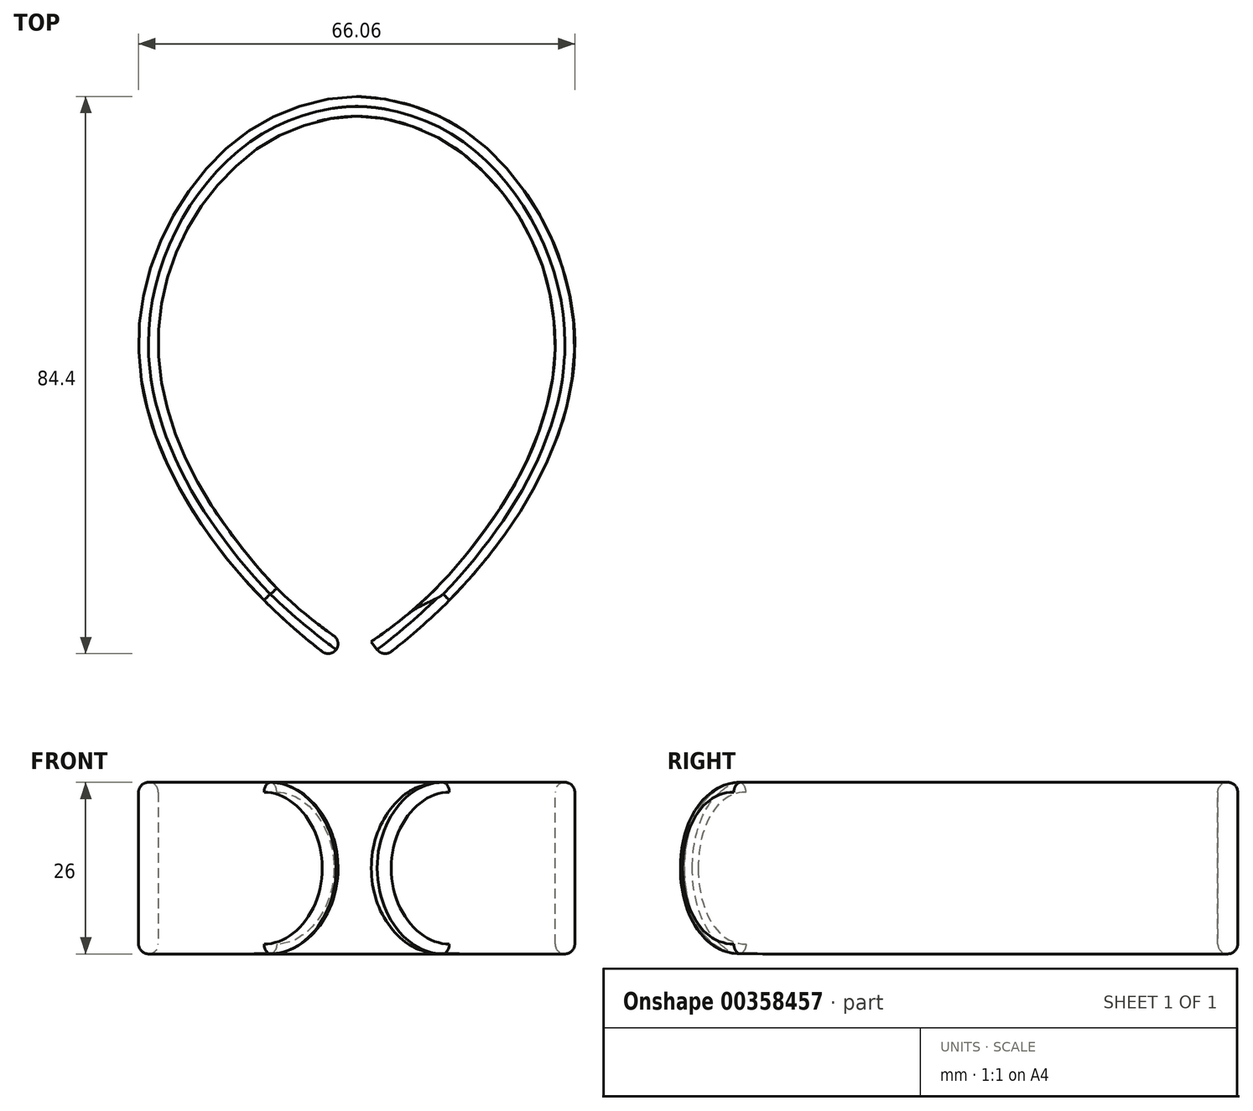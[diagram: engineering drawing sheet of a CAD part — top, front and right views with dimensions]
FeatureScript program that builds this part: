
annotation { "Feature Type Name" : "Feature", "Feature Type Description" : "" }
export const myFeature = defineFeature(function(context is Context, id is Id, definition is map)
    precondition{}
    {
        {
            var Q0;
            Q0=qCreatedBy(makeId("Top.planeOp"),FACE);
            var sketch = newSketch(context, id + "F0", { "sketchPlane" : qUnion([Q0])});
            skFitSpline(sketch, "E0", {"points": [v(-4, -45.97) * mm, v(-33, 0) * mm, v(-16.4, 33.8) * mm, v(0, 39.03) * mm], "startDerivative": vector(-109.41, 80.65) * mm, "endDerivative": vector(42.57, 0) * mm});
            skLineSegment(sketch, "E1", {"start": v(-3.33, 39.03) * mm, "end": v(0, 39.03) * mm, "construction": true});
            skLineSegment(sketch, "E2", {"start": v(-4, -45.97) * mm, "end": v(0, -45.97) * mm, "construction": true});
            skFitSpline(sketch, "E3.0", {"points": [v(-2.22, -43.56) * mm, v(-6.61, -40.32) * mm, v(-12.94, -34.6) * mm, v(-20, -25.85) * mm, v(-24.39, -18.91) * mm, v(-27.13, -12.97) * mm, v(-28.69, -8.2) * mm, v(-29.52, -4.64) * mm, v(-29.9, -1.7) * mm, v(-30.04, 0.61) * mm, v(-30.04, 2.92) * mm, v(-29.8, 5.8) * mm, v(-29, 10.3) * mm, v(-27.22, 15.74) * mm, v(-24.07, 21.67) * mm, v(-20.82, 25.92) * mm, v(-18, 28.77) * mm, v(-15.8, 30.61) * mm, v(-13.56, 32.12) * mm, v(-11.29, 33.33) * mm, v(-9.02, 34.29) * mm, v(-6.1, 35.24) * mm, v(-3.42, 35.77) * mm, v(-1.24, 36) * mm, v(-0.37, 36.03) * mm, v(0, 36.03) * mm]});
            skLineSegment(sketch, "E4", {"start": v(-2.22, -43.56) * mm, "end": v(-4, -45.97) * mm});
            skFitSpline(sketch, "E5.MirrorCS", {"points": [v(4, -45.97) * mm, v(33, 0) * mm, v(16.4, 33.8) * mm, v(0, 39.03) * mm], "startDerivative": vector(109.41, 80.65) * mm, "endDerivative": vector(-42.57, 0) * mm});
            skLineSegment(sketch, "E6.MirrorCS", {"start": v(2.22, -43.56) * mm, "end": v(4, -45.97) * mm});
            skFitSpline(sketch, "E7.0", {"points": [v(2.22, -43.56) * mm, v(6.61, -40.32) * mm, v(12.94, -34.6) * mm, v(20, -25.85) * mm, v(24.39, -18.91) * mm, v(27.13, -12.97) * mm, v(28.69, -8.2) * mm, v(29.52, -4.64) * mm, v(29.9, -1.7) * mm, v(30.04, 0.61) * mm, v(30.04, 2.92) * mm, v(29.8, 5.8) * mm, v(29, 10.3) * mm, v(27.22, 15.74) * mm, v(24.07, 21.67) * mm, v(20.82, 25.92) * mm, v(18, 28.77) * mm, v(15.8, 30.61) * mm, v(13.56, 32.12) * mm, v(11.29, 33.33) * mm, v(9.02, 34.29) * mm, v(6.1, 35.24) * mm, v(3.42, 35.77) * mm, v(1.24, 36) * mm, v(0.37, 36.03) * mm, v(0, 36.03) * mm]});
            skSolve(sketch);
        }
        {
            var Q0;
            Q0 = qSketchRegion(id + "F0", true);
            extrude(context, id + "F1", {"entities" : qUnion([Q0]), "depth" : 26 * mm});
        }
        {
            var Q0;
            Q0=makeQuery(id+"F1.opExtrude","CAP_EDGE",EDGE,{"disambiguationData":[OSD([sQuery(id+"F0.wireOp",EDGE,"E4")])],"isStart":false});
            var Q1;
            Q1=makeQuery(id+"F1.opExtrude","CAP_EDGE",EDGE,{"disambiguationData":[OSD([sQuery(id+"F0.wireOp",EDGE,"E6.MirrorCS")])],"isStart":false});
            var Q2;
            Q2=makeQuery(id+"F1.opExtrude","CAP_EDGE",EDGE,{"disambiguationData":[OSD([sQuery(id+"F0.wireOp",EDGE,"E4")])],"isStart":true});
            var Q3;
            Q3=makeQuery(id+"F1.opExtrude","CAP_EDGE",EDGE,{"disambiguationData":[OSD([sQuery(id+"F0.wireOp",EDGE,"E6.MirrorCS")])],"isStart":true});
            fillet(context, id + "F2", {"entities" : qUnion([Q0, Q1, Q2, Q3]), "radius" : 13 * mm, "tangentPropagation" : true, "allowEdgeOverflow" : false});
        }
        {
            var Q0;
            Q0=makeQuery(id+"F1.opExtrude","CAP_EDGE",EDGE,{"disambiguationData":[OSD([sQuery(id+"F0.wireOp",EDGE,"E0")])],"isStart":false});
            var Q1;
            Q1=makeQuery(id+"F1.opExtrude","CAP_EDGE",EDGE,{"disambiguationData":[OSD([sQuery(id+"F0.wireOp",EDGE,"E3.0")])],"isStart":false});
            fillet(context, id + "F3", {"entities" : qUnion([Q0, Q1]), "radius" : 1.49 * mm, "tangentPropagation" : true, "allowEdgeOverflow" : false});
        }
    });
